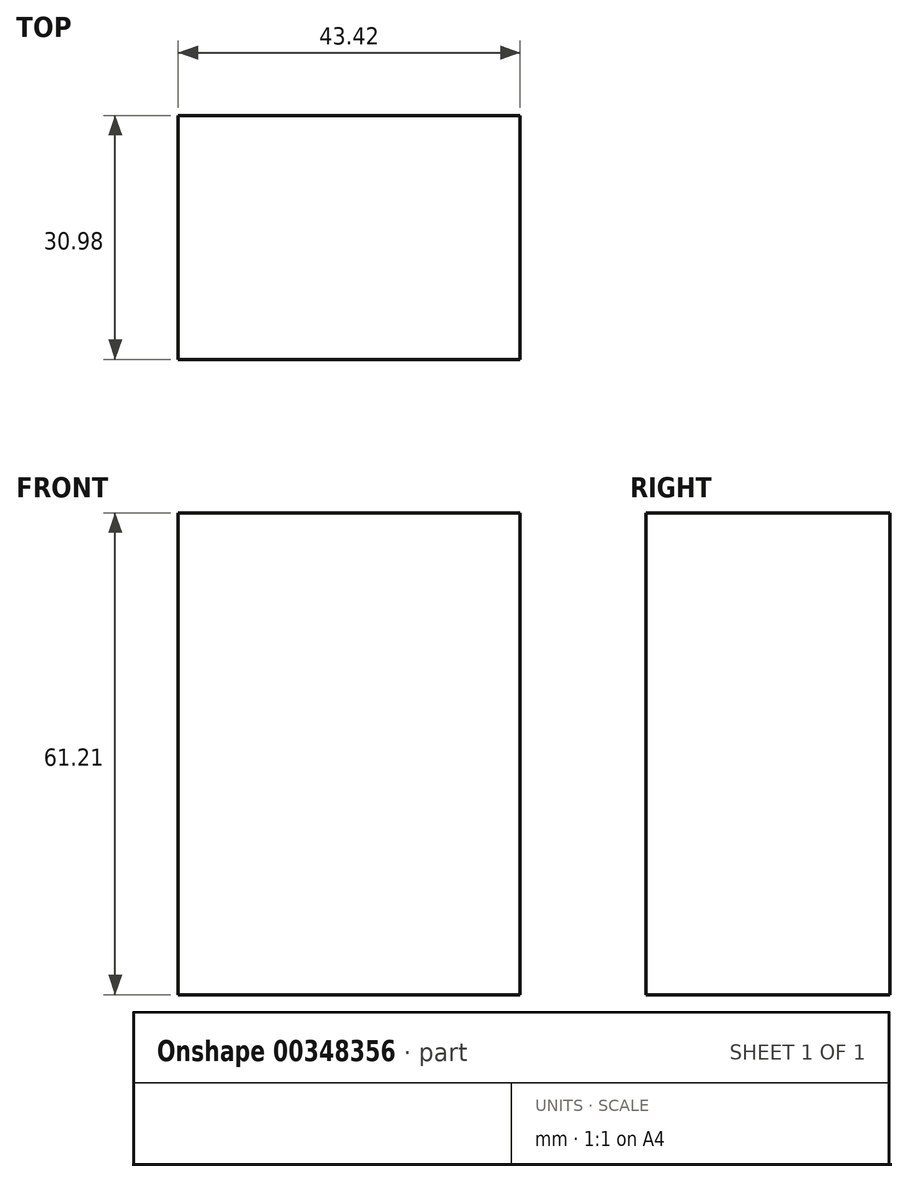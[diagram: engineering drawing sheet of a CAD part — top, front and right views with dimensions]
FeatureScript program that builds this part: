
annotation { "Feature Type Name" : "Feature", "Feature Type Description" : "" }
export const myFeature = defineFeature(function(context is Context, id is Id, definition is map)
    precondition{}
    {
        {
            var Q0;
            Q0=qCreatedBy(makeId("Top.planeOp"),FACE);
            var sketch = newSketch(context, id + "F0", { "sketchPlane" : qUnion([Q0])});
            skLineSegment(sketch, "E0", {"start": v(-60.6, -32.23) * mm, "end": v(-3.31, 27.63) * mm});
            skLineSegment(sketch, "E1.bottom", {"start": v(-29.75, -15.03) * mm, "end": v(13.67, -15.03) * mm});
            skLineSegment(sketch, "E1.top", {"start": v(-29.75, -46.01) * mm, "end": v(13.67, -46.01) * mm});
            skLineSegment(sketch, "E1.left", {"start": v(-29.75, -15.03) * mm, "end": v(-29.75, -46.01) * mm});
            skLineSegment(sketch, "E1.right", {"start": v(13.67, -15.03) * mm, "end": v(13.67, -46.01) * mm});
            skSolve(sketch);
        }
        {
            var Q0;
            Q0=makeQuery(id+"F0.imprint","IMPRINT",FACE,{"disambiguationData":[TD([[makeQuery(id+"F0.imprint","IMPRINT",EDGE,{"derivedFrom":sQuery(id+"F0.wireOp",EDGE,"E1.bottom")}),-1.0]])]});
            extrude(context, id + "F1", {"entities" : qUnion([Q0]), "depth" : 61.2 * mm, "offsetDistance" : 25.4 * mm});
        }
    });
